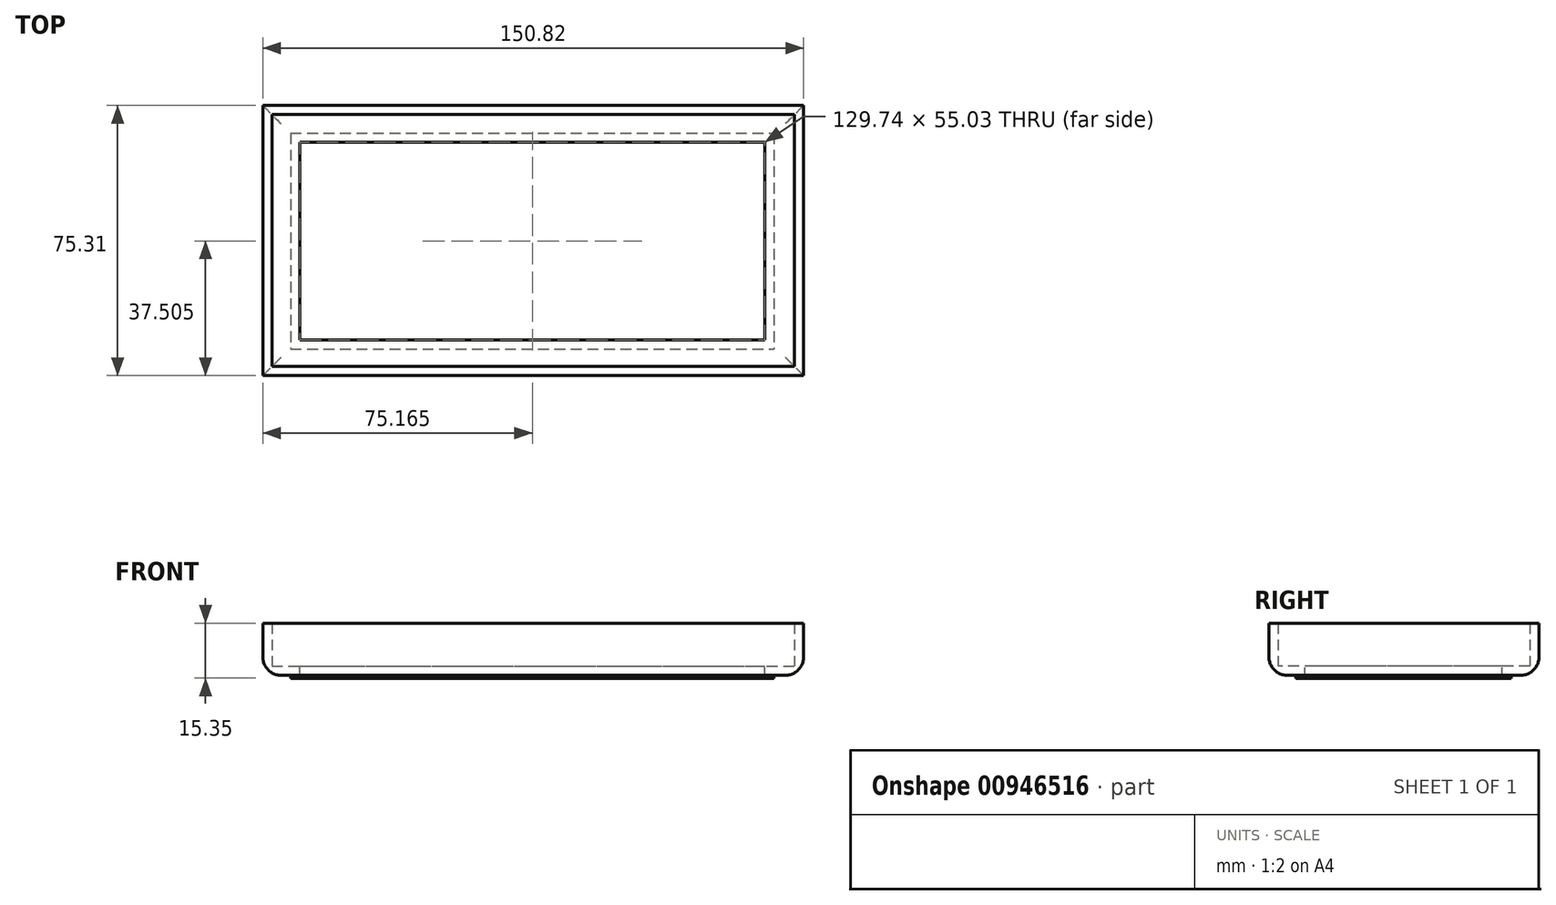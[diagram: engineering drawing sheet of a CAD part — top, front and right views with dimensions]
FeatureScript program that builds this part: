
annotation { "Feature Type Name" : "Feature", "Feature Type Description" : "" }
export const myFeature = defineFeature(function(context is Context, id is Id, definition is map)
    precondition{}
    {
        {
            var Q0;
            Q0=qCreatedBy(makeId("Top.planeOp"),FACE);
            var sketch = newSketch(context, id + "F0", { "sketchPlane" : qUnion([Q0])});
            skLineSegment(sketch, "E0.bottom", {"start": v(0, 0) * mm, "end": v(150.82, 0) * mm});
            skLineSegment(sketch, "E0.top", {"start": v(0, -75.3) * mm, "end": v(150.82, -75.3) * mm});
            skLineSegment(sketch, "E0.left", {"start": v(0, 0) * mm, "end": v(0, -75.3) * mm});
            skLineSegment(sketch, "E0.right", {"start": v(150.82, 0) * mm, "end": v(150.82, -75.3) * mm});
            skSolve(sketch);
        }
        {
            var Q0;
            Q0=makeQuery(id+"F0.imprint","IMPRINT",FACE,{"disambiguationData":[TD([[makeQuery(id+"F0.imprint","IMPRINT",EDGE,{"derivedFrom":sQuery(id+"F0.wireOp",EDGE,"E0.bottom")}),-1.0]])]});
            extrude(context, id + "F1", {"entities" : qUnion([Q0]), "depth" : 14.54 * mm, "offsetDistance" : 25.4 * mm});
        }
        {
            var Q0;
            Q0=makeQuery(id+"F1.opExtrude","CAP_FACE",FACE,{"disambiguationData":[OSD([sQuery(id+"F0.wireOp",EDGE,"E0.bottom"),sQuery(id+"F0.wireOp",EDGE,"E0.top"),sQuery(id+"F0.wireOp",EDGE,"E0.left"),sQuery(id+"F0.wireOp",EDGE,"E0.right")])],"isStart":false});
            var sketch = newSketch(context, id + "F2", { "sketchPlane" : qUnion([Q0])});
            skLineSegment(sketch, "E1.bottom", {"start": v(7.75, -7.75) * mm, "end": v(142.58, -7.75) * mm});
            skLineSegment(sketch, "E1.top", {"start": v(7.75, -67.86) * mm, "end": v(142.58, -67.86) * mm});
            skLineSegment(sketch, "E1.left", {"start": v(7.75, -7.75) * mm, "end": v(7.75, -67.86) * mm});
            skLineSegment(sketch, "E1.right", {"start": v(142.58, -7.75) * mm, "end": v(142.58, -67.86) * mm});
            skSolve(sketch);
        }
        {
            var Q0;
            Q0=makeQuery(id+"F2.imprint","IMPRINT",FACE,{"disambiguationData":[TD([[makeQuery(id+"F2.imprint","IMPRINT",EDGE,{"derivedFrom":sQuery(id+"F2.wireOp",EDGE,"E1.bottom")}),-1.0]])]});
            extrude(context, id + "F3", {"entities" : qUnion([Q0]), "operationType" : NewBodyOperationType.ADD, "oppositeDirection" : true, "depth" : 15.35 * mm, "offsetDistance" : 25.4 * mm});
        }
        {
            var Q0;
            Q0=makeQuery(id+"F3.opExtrude","CAP_FACE",FACE,{"disambiguationData":[OSD([sQuery(id+"F2.wireOp",EDGE,"E1.bottom"),sQuery(id+"F2.wireOp",EDGE,"E1.top"),sQuery(id+"F2.wireOp",EDGE,"E1.left"),sQuery(id+"F2.wireOp",EDGE,"E1.right")])],"isStart":false});
            var Q1;
            Q1=makeQuery(id+"F1.opExtrude","CAP_FACE",FACE,{"disambiguationData":[OSD([sQuery(id+"F0.wireOp",EDGE,"E0.bottom"),sQuery(id+"F0.wireOp",EDGE,"E0.top"),sQuery(id+"F0.wireOp",EDGE,"E0.left"),sQuery(id+"F0.wireOp",EDGE,"E0.right")])],"isStart":false});
            shell(context, id + "F4", {"entities" : qUnion([Q0, Q1]), "thickness" : 2.54 * mm});
        }
        {
            var Q0;
            Q0=makeQuery(id+"F1.opExtrude","CAP_EDGE",EDGE,{"disambiguationData":[OSD([sQuery(id+"F0.wireOp",EDGE,"E0.top")])],"isStart":true});
            var Q1;
            Q1=makeQuery(id+"F1.opExtrude","CAP_EDGE",EDGE,{"disambiguationData":[OSD([sQuery(id+"F0.wireOp",EDGE,"E0.bottom")])],"isStart":true});
            var Q2;
            Q2=makeQuery(id+"F1.opExtrude","CAP_EDGE",EDGE,{"disambiguationData":[OSD([sQuery(id+"F0.wireOp",EDGE,"E0.right")])],"isStart":true});
            var Q3;
            Q3=makeQuery(id+"F1.opExtrude","CAP_EDGE",EDGE,{"disambiguationData":[OSD([sQuery(id+"F0.wireOp",EDGE,"E0.left")])],"isStart":true});
            fillet(context, id + "F5", {"entities" : qUnion([Q0, Q1, Q2, Q3]), "radius" : 5.08 * mm, "tangentPropagation" : true, "allowEdgeOverflow" : false});
        }
    });
